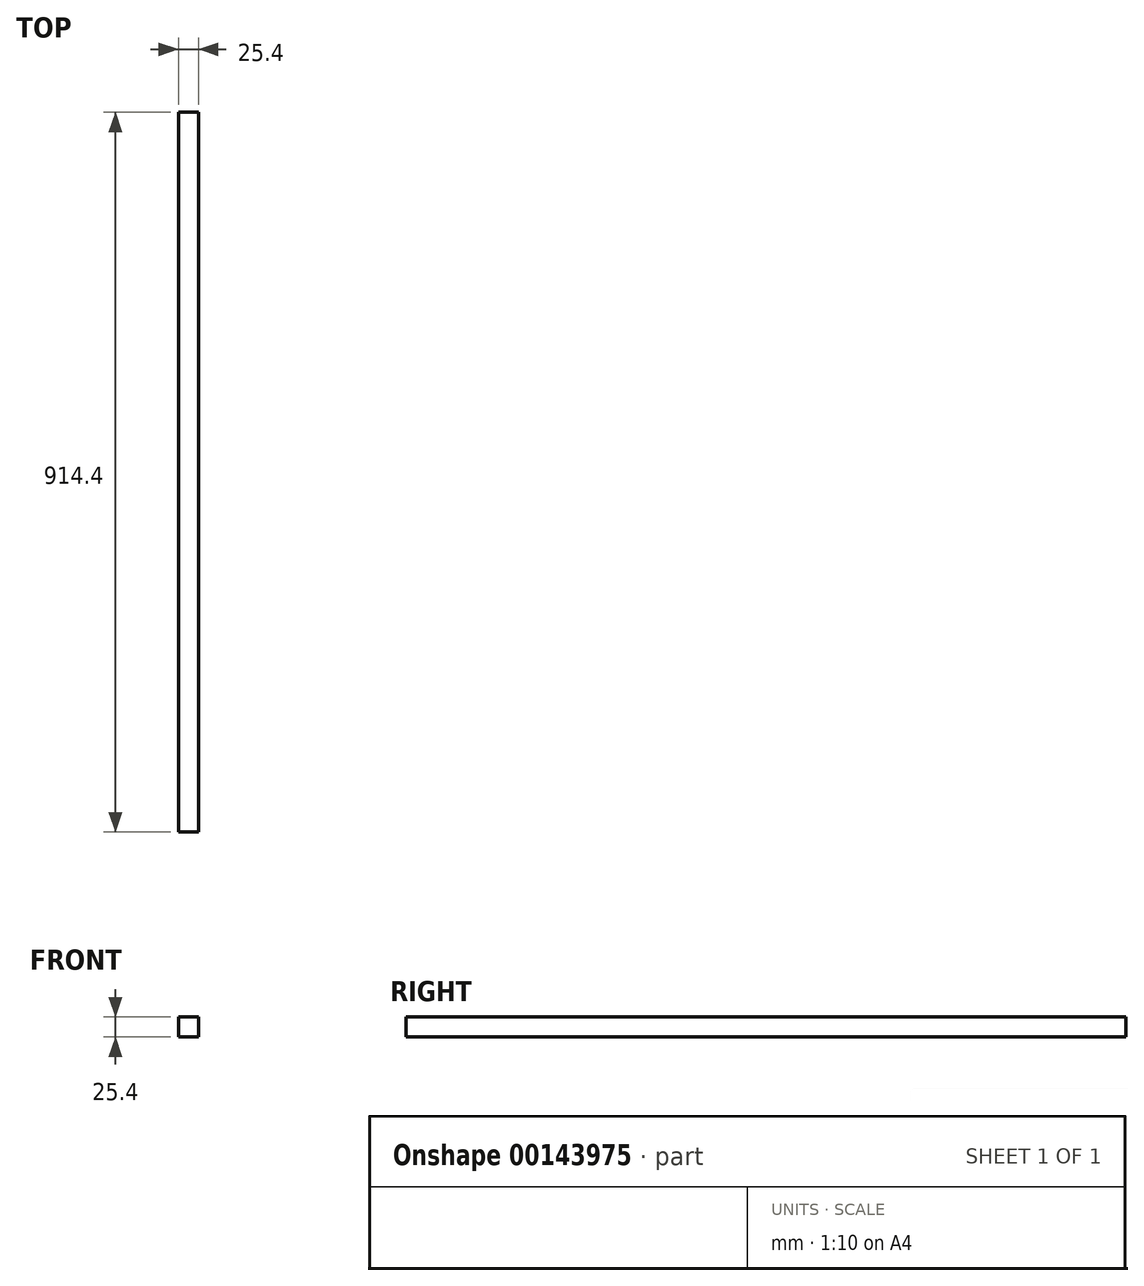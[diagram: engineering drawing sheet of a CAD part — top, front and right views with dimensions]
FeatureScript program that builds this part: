
annotation { "Feature Type Name" : "Feature", "Feature Type Description" : "" }
export const myFeature = defineFeature(function(context is Context, id is Id, definition is map)
    precondition{}
    {
        {
            var Q0;
            Q0=qCreatedBy(makeId("Front.planeOp"),FACE);
            var sketch = newSketch(context, id + "F0", { "sketchPlane" : qUnion([Q0])});
            skLineSegment(sketch, "E0.bottom", {"start": v(0, 0) * mm, "end": v(25.4, 0) * mm});
            skLineSegment(sketch, "E0.top", {"start": v(0, 25.4) * mm, "end": v(25.4, 25.4) * mm});
            skLineSegment(sketch, "E0.left", {"start": v(0, 0) * mm, "end": v(0, 25.4) * mm});
            skLineSegment(sketch, "E0.right", {"start": v(25.4, 0) * mm, "end": v(25.4, 25.4) * mm});
            skSolve(sketch);
        }
        {
            var Q0;
            Q0 = qSketchRegion(id + "F0", true);
            extrude(context, id + "F1", {"entities" : qUnion([Q0]), "depth" : 914.4 * mm});
        }
    });
